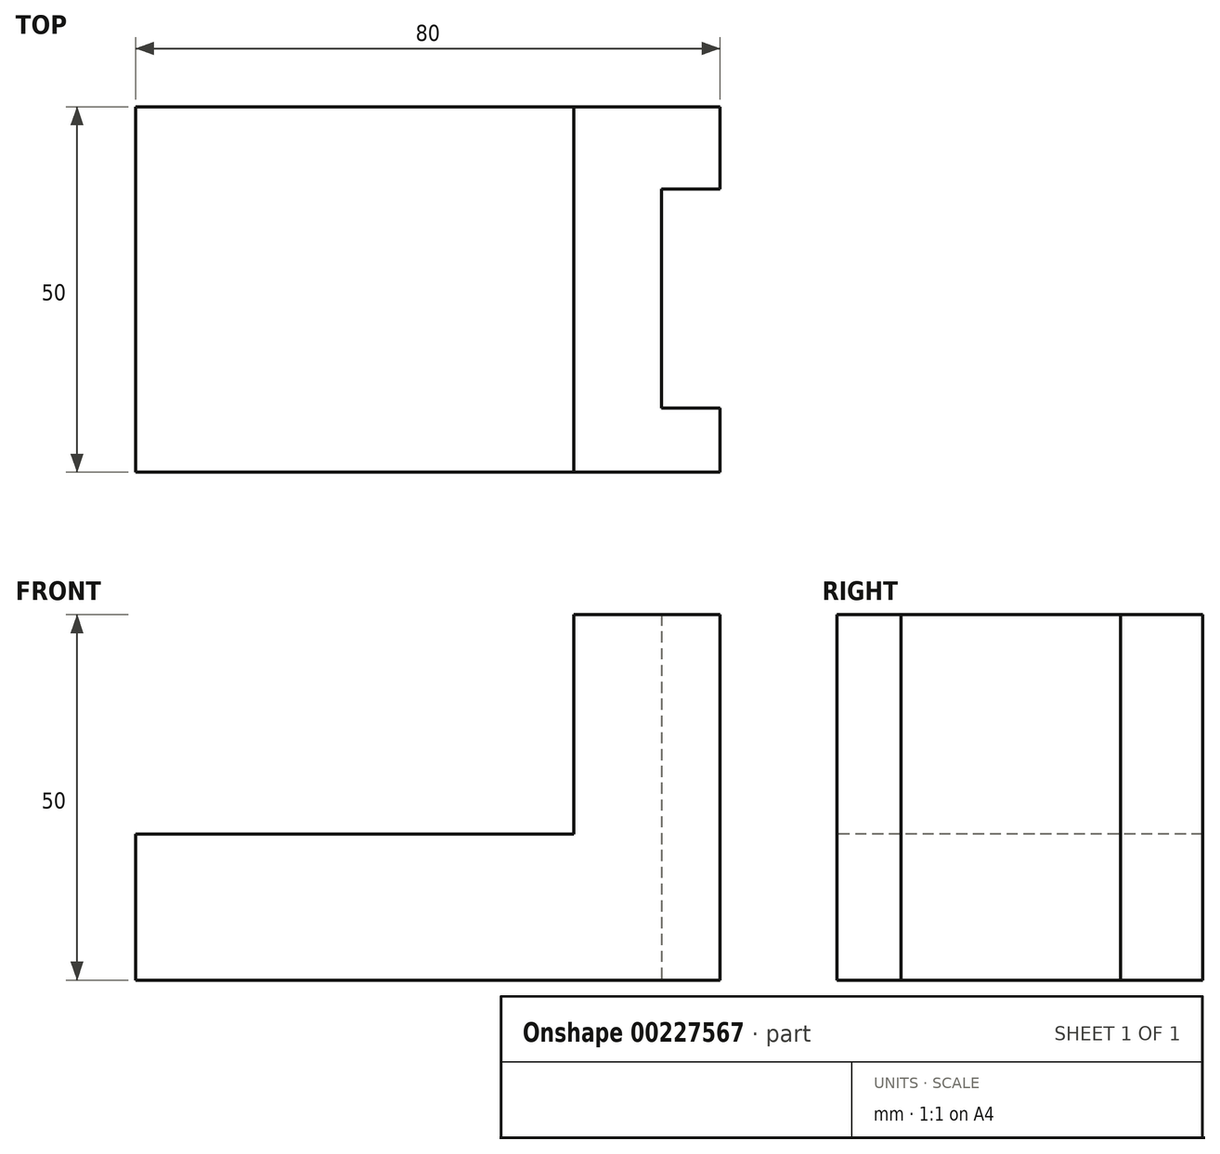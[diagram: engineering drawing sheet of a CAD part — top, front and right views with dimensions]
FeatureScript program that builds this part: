
annotation { "Feature Type Name" : "Feature", "Feature Type Description" : "" }
export const myFeature = defineFeature(function(context is Context, id is Id, definition is map)
    precondition{}
    {
        {
            var Q0;
            Q0=qCreatedBy(makeId("Top.planeOp"),FACE);
            var sketch = newSketch(context, id + "F0", { "sketchPlane" : qUnion([Q0])});
            skLineSegment(sketch, "E0", {"start": v(0, 0) * mm, "end": v(80, 0) * mm});
            skLineSegment(sketch, "E1", {"start": v(80, 0) * mm, "end": v(80, 8.76) * mm});
            skLineSegment(sketch, "E2", {"start": v(80, 8.76) * mm, "end": v(72, 8.76) * mm});
            skLineSegment(sketch, "E3", {"start": v(72, 8.76) * mm, "end": v(72, 38.76) * mm});
            skLineSegment(sketch, "E4", {"start": v(72, 38.76) * mm, "end": v(80, 38.76) * mm});
            skLineSegment(sketch, "E5", {"start": v(80, 38.76) * mm, "end": v(80, 50) * mm});
            skLineSegment(sketch, "E6", {"start": v(80, 50) * mm, "end": v(0, 50) * mm});
            skLineSegment(sketch, "E7", {"start": v(0, 50) * mm, "end": v(0, 0) * mm});
            skLineSegment(sketch, "E8", {"start": v(60, 50) * mm, "end": v(60, 0) * mm});
            skSolve(sketch);
        }
        {
            var Q0;
            {var subQ0=sQuery(id+"F0.wireOp",EDGE,"E7");Q0=makeQuery(id+"F0.imprint","IMPRINT",FACE,{"disambiguationData":[TD([[makeQuery(id+"F0.imprint","IMPRINT",EDGE,{"derivedFrom":subQ0}),1.0]])]});}
            extrude(context, id + "F1", {"entities" : qUnion([Q0]), "depth" : 20 * mm});
        }
        {
            var Q0;
            {var subQ1=sQuery(id+"F0.wireOp",EDGE,"E1");Q0=makeQuery(id+"F0.imprint","IMPRINT",FACE,{"disambiguationData":[TD([[makeQuery(id+"F0.imprint","IMPRINT",EDGE,{"derivedFrom":subQ1}),1.0]])]});}
            extrude(context, id + "F2", {"entities" : qUnion([Q0]), "operationType" : NewBodyOperationType.ADD, "depth" : 50 * mm});
        }
    });
